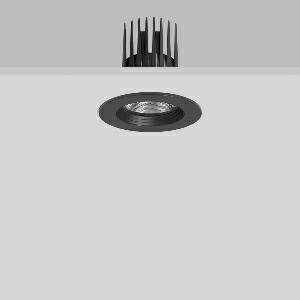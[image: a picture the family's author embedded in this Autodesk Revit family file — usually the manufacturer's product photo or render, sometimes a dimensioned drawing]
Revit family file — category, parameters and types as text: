
# Revit family: heledon_mini_e_901740_003_2_7698
name_source: partatom
category: Lighting Fixtures
units: mm (PartAtom-declared; Revit-internal decimal feet)

## family parameters
Cut with Voids When Loaded = No
Host = Face
Light Source = No
Part Type = Normal
Room Calculation Point = No
Round Connector Dimension = Use Diameter
Shared = No

## types (1)
- HELEDON mini E (1 x LED Modul 927, 2400 lm, 2700)
    Apparent Load = 20 VA
    Approval mark = CE
    CIE Flux Codes = 100 100 100 100 100
    Color Rendering = 92
    Color Temperature = 2700
    Default Elevation = 1800 mm
    Description = Series: HELEDON mini
Round recessed downlight. Housing: die-cast aluminium, powder-coated. Black plastic ring and recessed LED to prevent glare from the side. Optical assembly with reflector made of MIRO-Silver with 98% total light reflection for outstanding efficiency - can be changed without tools. Best colour rendering index Ra>90. Suitable for Recessed ceiling mounting. Installation without tools thanks to spring fastening system. Including separate LED converter with connecting cable 600 mm.High quality converter without flickering and stroboscopic effect. Through-wiring box (5 pole) available as accessory. The following accessories can be mounted without use of tools: interchangeable lenses, decorative glasses, honeycomb louvre, clear and frosted diffusers, white interchangeable plastic ring. 
Colour: deep black, matt (RAL 9005)
Diameter: 124 mm
Height: 3 mm
Cut-out diameter: 114 mm
Recess height: 170 mm
Luminaire: recess height: 120 mm
Lamp: LED
Socket: without socket
Colour temperature: 2700K
Colour rendering index (CRI): 92
System power: 20 W
Rated luminous flux: 2400 lm
Luminous efficiency: 120 lm/W
Control gear: Regulated power supply
Protection class: II
Type of protection: IP 20
    Height = 0 mm  [stored 0 ft]
    Lamp = 1 x LED Modul 927
    Lamp Light Flux = 2400 lm
    Lamp count = 1
    Length = 124 mm  [stored 0.406824 ft]
    Lifetime = 50000 h
    Luminous efficacy = 120 lm/W
    Manufacturer = RZB
    ModVariant = No
    Model = 901740.003.2
    Mounting Place = Ceiling
    Mounting Type = Recessed
    Number of Poles = 1
    OnlyDefault = Yes
    Power Factor = 1
    Product Name = HELEDON mini E
    Product group = Recessed downlights
    ProductGroupID = 402
    Protection Class = Protection class II
    Protection Degree = IP 20
    RLX_Detail_Level = 1
    RLX_Emergency_Light_Flux = 0 lm
    RLX_Emergency_Type = 0
    RLX_Emergency_Type_DB = No
    RlxData = <blob elided: 126369 chars, md5=ca879f74>
    Socket = socket
    Standby Power = 0 W
    System Light Flux = 2400 lm
    System Power = 20 W
    Type Comments = Product without accessories
    Type Image = 901657.003.jpg
    URL = http://relux.com
    VarID = ---
    Voltage = 230 V
    Voltage Range = 220-240 V
    Weight = 0.00 kg
    Width = 0 mm  [stored 0 ft]

note: [stored X ft] marks values corroborated as IEEE doubles in the binary element streams (Revit-internal decimal feet)

## geometry (parser evidence)
native form markers: Blend x4, Sweep x11
no freeform markers — native parametric forms only
